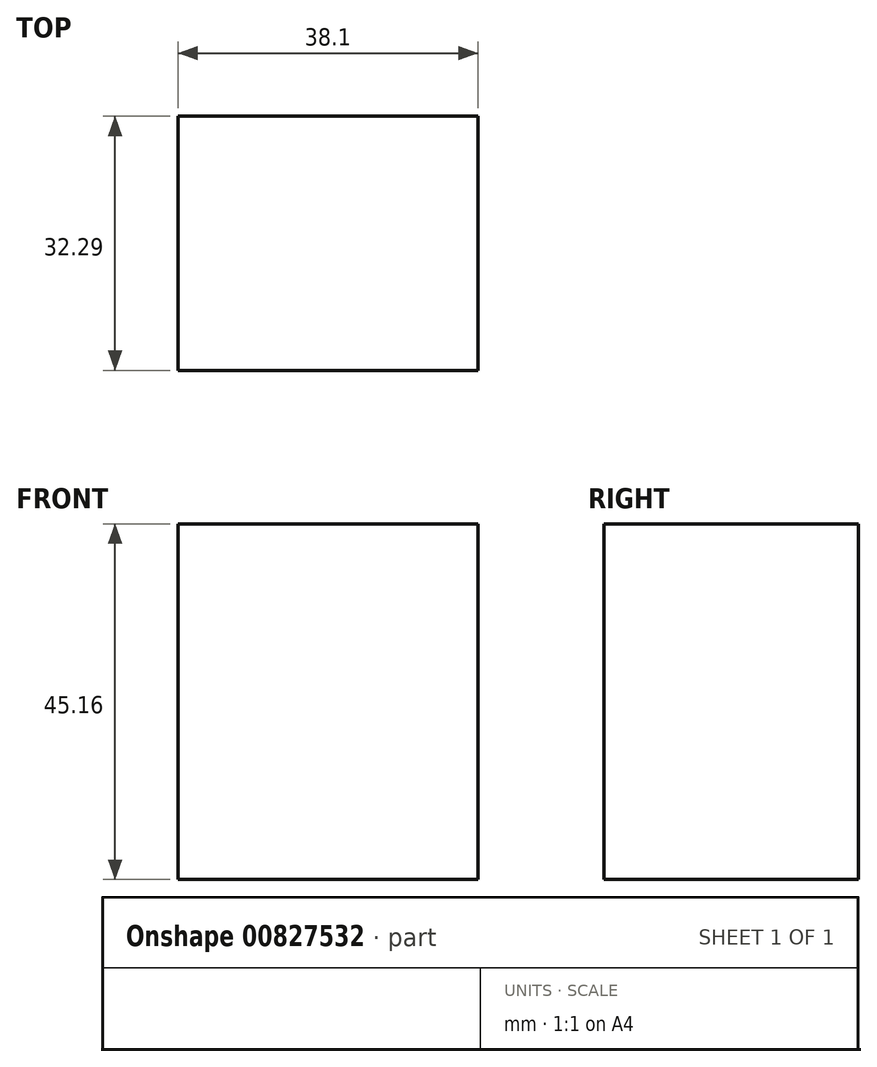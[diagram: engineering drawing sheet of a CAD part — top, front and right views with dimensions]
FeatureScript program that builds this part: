
annotation { "Feature Type Name" : "Feature", "Feature Type Description" : "" }
export const myFeature = defineFeature(function(context is Context, id is Id, definition is map)
    precondition{}
    {
        {
            var Q0;
            Q0=qCreatedBy(makeId("Right.planeOp"),FACE);
            var sketch = newSketch(context, id + "F0", { "sketchPlane" : qUnion([Q0])});
            skLineSegment(sketch, "E0.bottom", {"start": v(0, 0) * mm, "end": v(32.3, 0) * mm});
            skLineSegment(sketch, "E0.top", {"start": v(0, 45.16) * mm, "end": v(32.3, 45.16) * mm});
            skLineSegment(sketch, "E0.left", {"start": v(0, 0) * mm, "end": v(0, 45.16) * mm});
            skLineSegment(sketch, "E0.right", {"start": v(32.3, 0) * mm, "end": v(32.3, 45.16) * mm});
            skSolve(sketch);
        }
        {
            var Q0;
            Q0=makeQuery(id+"F0.imprint","IMPRINT",FACE,{"disambiguationData":[TD([[makeQuery(id+"F0.imprint","IMPRINT",EDGE,{"derivedFrom":sQuery(id+"F0.wireOp",EDGE,"E0.bottom")}),1.0]])]});
            extrude(context, id + "F1", {"entities" : qUnion([Q0]), "depth" : 38.1 * mm, "offsetDistance" : 25.4 * mm});
        }
    });
